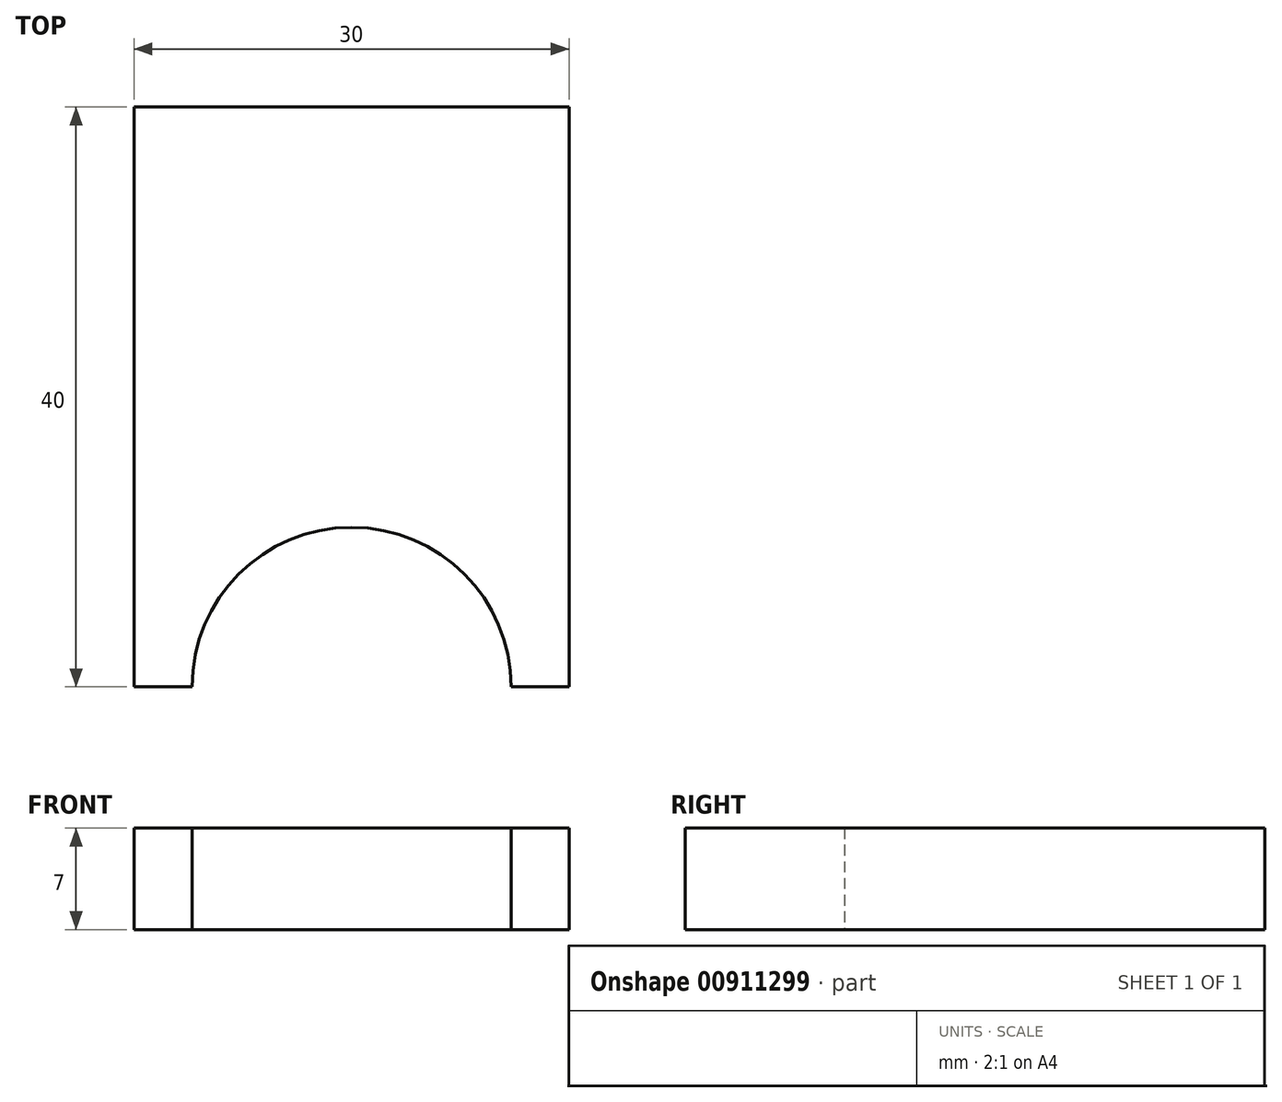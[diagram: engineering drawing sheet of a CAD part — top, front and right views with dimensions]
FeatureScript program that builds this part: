
annotation { "Feature Type Name" : "Feature", "Feature Type Description" : "" }
export const myFeature = defineFeature(function(context is Context, id is Id, definition is map)
    precondition{}
    {
        {
            var Q0;
            Q0=qCreatedBy(makeId("Top.planeOp"),FACE);
            var sketch = newSketch(context, id + "F0", { "sketchPlane" : qUnion([Q0])});
            skCircle(sketch, "E0", {"center": v(0, 0) * mm, "radius": 11 * mm});
            skLineSegment(sketch, "E1", {"start": v(0, 0) * mm, "end": v(0, 40) * mm});
            skLineSegment(sketch, "E2", {"start": v(0, 40) * mm, "end": v(15, 40) * mm});
            skLineSegment(sketch, "E3", {"start": v(15, 40) * mm, "end": v(15, 0) * mm});
            skLineSegment(sketch, "E4", {"start": v(15, 0) * mm, "end": v(0, 0) * mm});
            skLineSegment(sketch, "E5", {"start": v(0, 0) * mm, "end": v(-15, 0) * mm});
            skLineSegment(sketch, "E6", {"start": v(-15, 0) * mm, "end": v(-15, 40) * mm});
            skLineSegment(sketch, "E7", {"start": v(-15, 40) * mm, "end": v(0, 40) * mm});
            skLineSegment(sketch, "E8", {"start": v(0, 40) * mm, "end": v(7.32, 40) * mm});
            skLineSegment(sketch, "E9", {"start": v(0, 40) * mm, "end": v(0, 0) * mm});
            skSolve(sketch);
        }
        {
            var Q0;
            Q0=makeQuery(id+"F0.imprint","IMPRINT",FACE,{"disambiguationData":[TD([[makeQuery(id+"F0.imprint","IMPRINT",EDGE,{"derivedFrom":sQuery(id+"F0.wireOp",EDGE,"E2")}),-1.0]])]});
            var Q1;
            {var subQ1=sQuery(id+"F0.wireOp",EDGE,"E6");Q1=makeQuery(id+"F0.imprint","IMPRINT",FACE,{"disambiguationData":[TD([[makeQuery(id+"F0.imprint","IMPRINT",EDGE,{"derivedFrom":subQ1}),-1.0]])]});}
            extrude(context, id + "F1", {"entities" : qUnion([Q0, Q1]), "depth" : 7 * mm, "offsetDistance" : 25 * mm});
        }
    });
